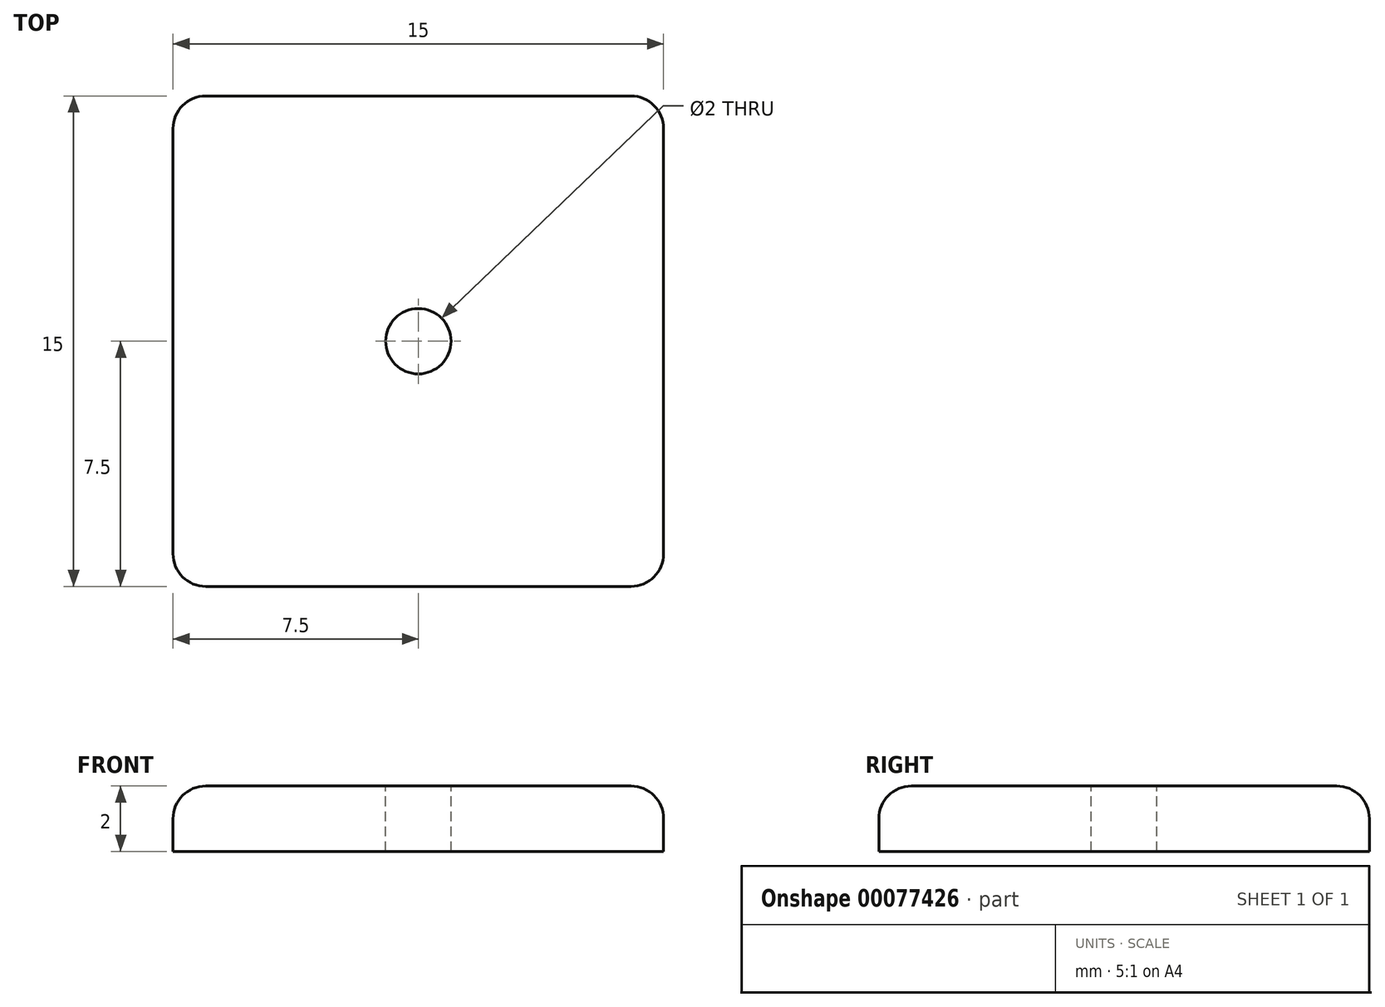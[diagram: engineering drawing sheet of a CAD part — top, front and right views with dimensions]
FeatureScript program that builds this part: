
annotation { "Feature Type Name" : "Feature", "Feature Type Description" : "" }
export const myFeature = defineFeature(function(context is Context, id is Id, definition is map)
    precondition{}
    {
        {
            var Q0;
            Q0=qCreatedBy(makeId("Top.planeOp"),FACE);
            var sketch = newSketch(context, id + "F0", { "sketchPlane" : qUnion([Q0])});
            skLineSegment(sketch, "E0.bottom", {"start": v(0, 0) * mm, "end": v(-15, 0) * mm});
            skLineSegment(sketch, "E0.top", {"start": v(0, 15) * mm, "end": v(-15, 15) * mm});
            skLineSegment(sketch, "E0.left", {"start": v(0, 0) * mm, "end": v(0, 15) * mm});
            skLineSegment(sketch, "E0.right", {"start": v(-15, 0) * mm, "end": v(-15, 15) * mm});
            skPoint(sketch, "E1", {"position": v(-7.5, 7.5) * mm});
            skSolve(sketch);
        }
        {
            var Q0;
            Q0 = qSketchRegion(id + "F0", true);
            extrude(context, id + "F1", {"entities" : qUnion([Q0]), "depth" : 2 * mm});
        }
        {
            var Q0;
            Q0=makeQuery(id+"F1.opExtrude","CAP_FACE",FACE,{"disambiguationData":[OSD([sQuery(id+"F0.wireOp",EDGE,"E0.bottom"),sQuery(id+"F0.wireOp",EDGE,"E0.top"),sQuery(id+"F0.wireOp",EDGE,"E0.left"),sQuery(id+"F0.wireOp",EDGE,"E0.right")])],"isStart":false});
            var sketch = newSketch(context, id + "F2", { "sketchPlane" : qUnion([Q0])});
            skPoint(sketch, "E2", {"position": v(-7.5, 7.5) * mm});
            skPoint(sketch, "E2.positionSnap0", {"position": v(0, 7.5) * mm});
            skPoint(sketch, "E2.positionSnap1", {"position": v(-7.5, 0) * mm});
            skSolve(sketch);
        }
        {
            var Q0;
            Q0=sQuery(id+"F2.wireOp",VERTEX,"E2");
            var Q1;
            Q1=makeQuery(id+"F1.opExtrude","SWEPT_BODY",BODY,{"disambiguationData":[OSD([sQuery(id+"F0.wireOp",EDGE,"E0.bottom"),sQuery(id+"F0.wireOp",EDGE,"E0.top"),sQuery(id+"F0.wireOp",EDGE,"E0.left"),sQuery(id+"F0.wireOp",EDGE,"E0.right")])]});
            hole(context, id + "F3", {"style" : HoleStyle.SIMPLE, "endStyle" : HoleEndStyle.THROUGH, "holeDiameter" : 2 * mm, "locations" : qUnion([Q0]), "scope" : qUnion([Q1]), "isTappedThrough" : true});
        }
        {
            var Q0;
            Q0=makeQuery(id+"F1.opExtrude","CAP_EDGE",EDGE,{"disambiguationData":[OSD([sQuery(id+"F0.wireOp",EDGE,"E0.bottom")])],"isStart":false});
            var Q1;
            Q1=makeQuery(id+"F1.opExtrude","CAP_EDGE",EDGE,{"disambiguationData":[OSD([sQuery(id+"F0.wireOp",EDGE,"E0.right")])],"isStart":false});
            var Q2;
            Q2=makeQuery(id+"F1.opExtrude","CAP_EDGE",EDGE,{"disambiguationData":[OSD([sQuery(id+"F0.wireOp",EDGE,"E0.top")])],"isStart":false});
            var Q3;
            Q3=makeQuery(id+"F1.opExtrude","CAP_EDGE",EDGE,{"disambiguationData":[OSD([sQuery(id+"F0.wireOp",EDGE,"E0.left")])],"isStart":false});
            var Q4;
            Q4=makeQuery(id+"F1.opExtrude","SWEPT_EDGE",EDGE,{"disambiguationData":[OSD([sQuery(id+"F0.wireOp",EDGE,"E0.bottom"),sQuery(id+"F0.wireOp",EDGE,"E0.left")])]});
            var Q5;
            Q5=makeQuery(id+"F1.opExtrude","SWEPT_EDGE",EDGE,{"disambiguationData":[OSD([sQuery(id+"F0.wireOp",EDGE,"E0.bottom"),sQuery(id+"F0.wireOp",EDGE,"E0.right")])]});
            var Q6;
            Q6=makeQuery(id+"F1.opExtrude","SWEPT_EDGE",EDGE,{"disambiguationData":[OSD([sQuery(id+"F0.wireOp",EDGE,"E0.top"),sQuery(id+"F0.wireOp",EDGE,"E0.left")])]});
            var Q7;
            Q7=makeQuery(id+"F1.opExtrude","SWEPT_EDGE",EDGE,{"disambiguationData":[OSD([sQuery(id+"F0.wireOp",EDGE,"E0.top"),sQuery(id+"F0.wireOp",EDGE,"E0.right")])]});
            fillet(context, id + "F4", {"entities" : qUnion([Q0, Q1, Q2, Q3, Q4, Q5, Q6, Q7]), "radius" : 1 * mm, "tangentPropagation" : true, "allowEdgeOverflow" : false});
        }
    });
